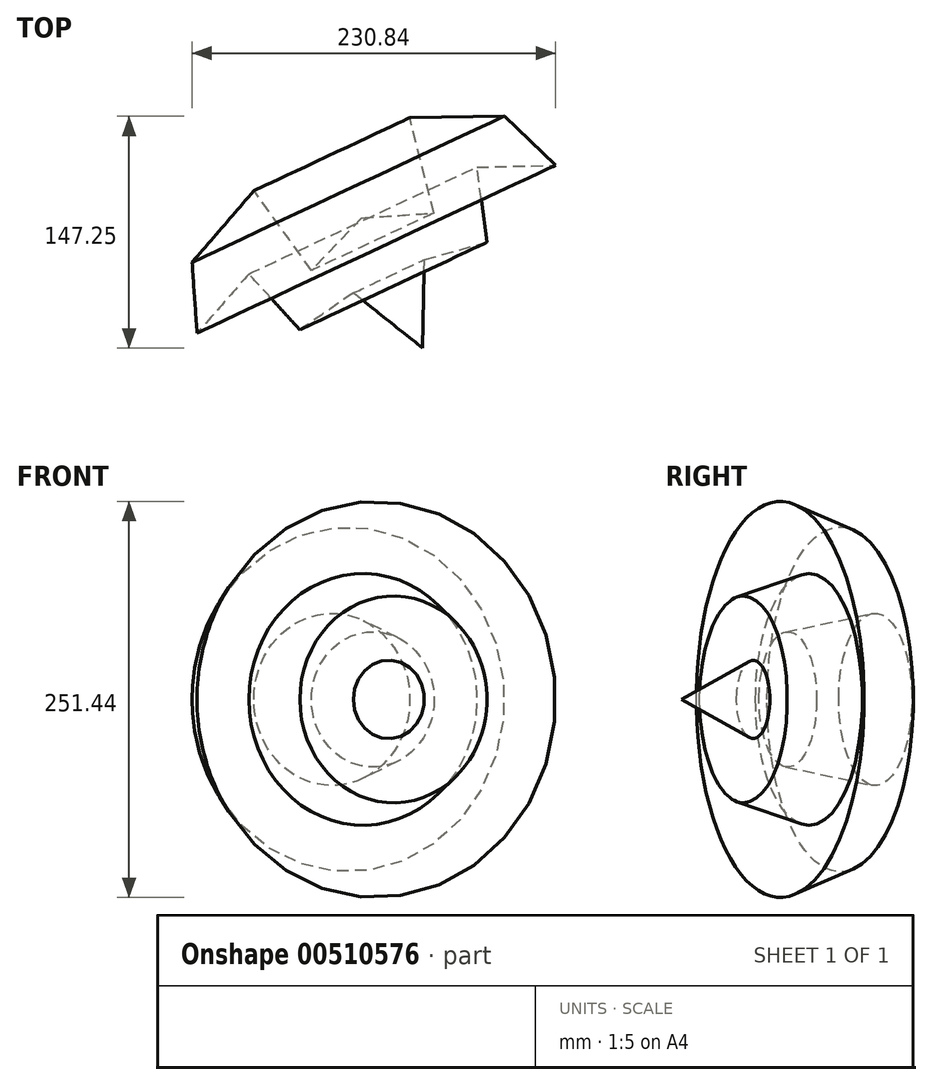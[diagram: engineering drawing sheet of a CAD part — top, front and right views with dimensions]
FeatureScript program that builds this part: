
annotation { "Feature Type Name" : "Feature", "Feature Type Description" : "" }
export const myFeature = defineFeature(function(context is Context, id is Id, definition is map)
    precondition{}
    {
        {
            var Q0;
            Q0=qCreatedBy(makeId("Top.planeOp"),FACE);
            var sketch = newSketch(context, id + "F0", { "sketchPlane" : qUnion([Q0])});
            skLineSegment(sketch, "E0", {"start": v(-47.55, 5.08) * mm, "end": v(-8.34, 50.56) * mm});
            skLineSegment(sketch, "E1", {"start": v(-8.34, 50.56) * mm, "end": v(28.25, 0) * mm});
            skLineSegment(sketch, "E2", {"start": v(28.25, 0) * mm, "end": v(60.14, 33.3) * mm});
            skLineSegment(sketch, "E3", {"start": v(60.14, 33.3) * mm, "end": v(98.82, -49.29) * mm});
            skLineSegment(sketch, "E4", {"start": v(98.82, -49.29) * mm, "end": v(54.9, -14.26) * mm});
            skLineSegment(sketch, "E5", {"start": v(54.9, -14.26) * mm, "end": v(20.93, -37.78) * mm});
            skLineSegment(sketch, "E6", {"start": v(20.93, -37.78) * mm, "end": v(-11.48, -2.24) * mm});
            skLineSegment(sketch, "E7", {"start": v(-11.48, -2.24) * mm, "end": v(-44.41, -39.88) * mm});
            skLineSegment(sketch, "E8", {"start": v(-44.41, -39.88) * mm, "end": v(-47.55, 5.08) * mm});
            skSolve(sketch);
        }
        {
            var Q0;
            Q0=makeQuery(id+"F0.imprint","IMPRINT",FACE,{"disambiguationData":[TD([[makeQuery(id+"F0.imprint","IMPRINT",EDGE,{"derivedFrom":sQuery(id+"F0.wireOp",EDGE,"E0")}),-1.0]])]});
            var Q1;
            Q1=sQuery(id+"F0.wireOp",EDGE,"E3");
            revolve(context, id + "F1", {"entities" : qUnion([Q0]), "axis" : qUnion([Q1]), "revolveType" : RevolveType.FULL});
        }
    });
